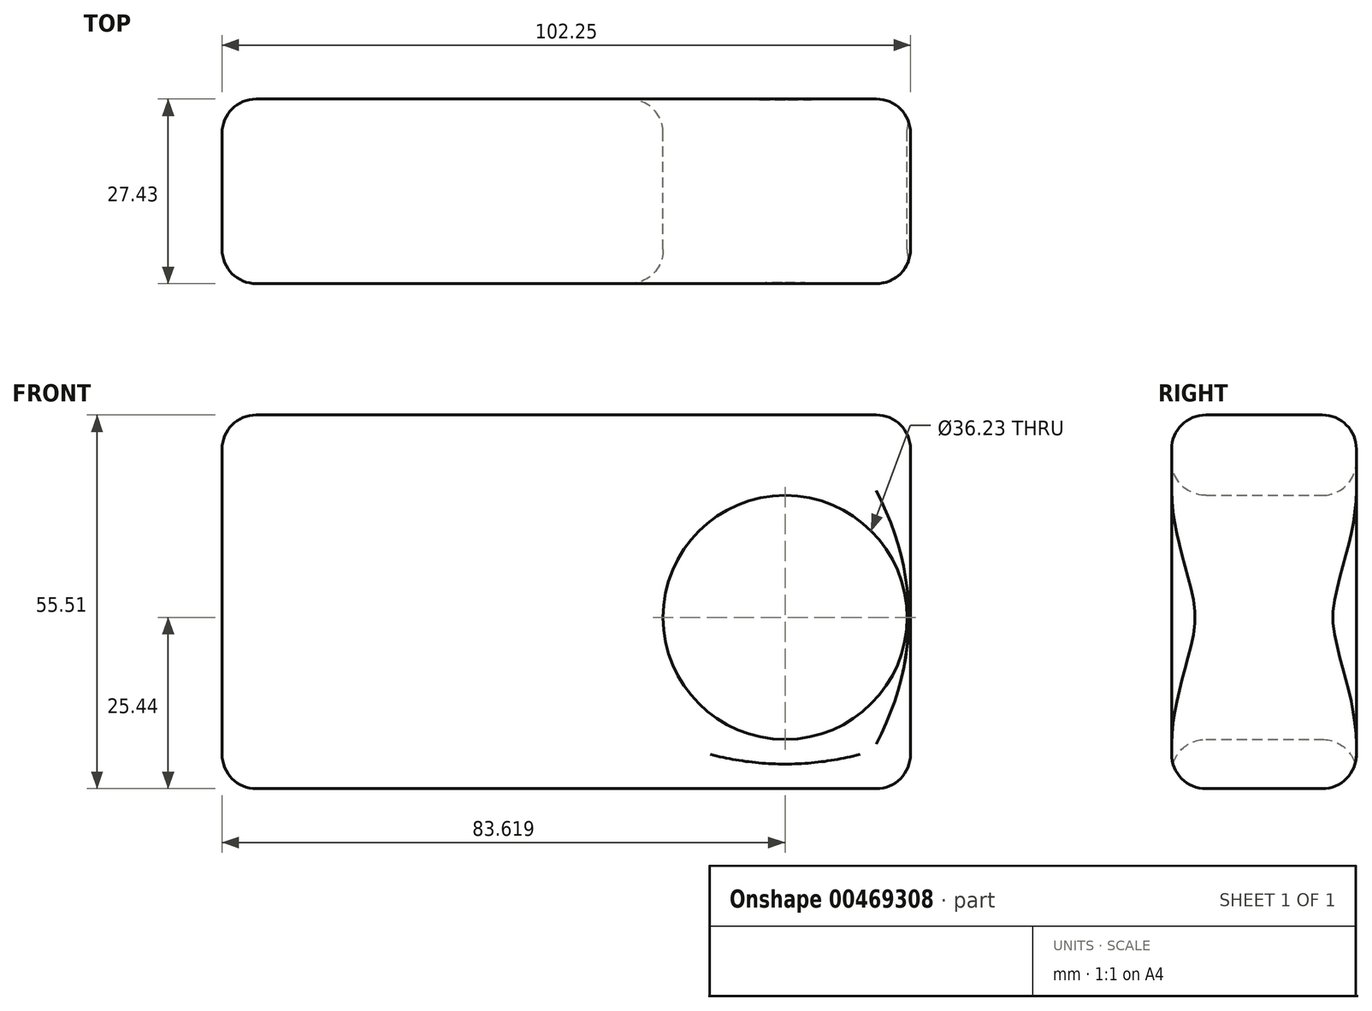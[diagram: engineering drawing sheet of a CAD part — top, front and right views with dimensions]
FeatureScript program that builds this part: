
annotation { "Feature Type Name" : "Feature", "Feature Type Description" : "" }
export const myFeature = defineFeature(function(context is Context, id is Id, definition is map)
    precondition{}
    {
        {
            var Q0;
            Q0=qCreatedBy(makeId("Front.planeOp"),FACE);
            var sketch = newSketch(context, id + "F0", { "sketchPlane" : qUnion([Q0])});
            skLineSegment(sketch, "E0.bottom", {"start": v(-64.67, 33.76) * mm, "end": v(37.58, 33.76) * mm});
            skLineSegment(sketch, "E0.top", {"start": v(-64.67, -21.75) * mm, "end": v(37.58, -21.75) * mm});
            skLineSegment(sketch, "E0.left", {"start": v(-64.67, 33.76) * mm, "end": v(-64.67, -21.75) * mm});
            skLineSegment(sketch, "E0.right", {"start": v(37.58, 33.76) * mm, "end": v(37.58, -21.75) * mm});
            skCircle(sketch, "E1", {"center": v(18.95, 3.7) * mm, "radius": 18.12 * mm});
            skSolve(sketch);
        }
        {
            var Q0;
            Q0 = qSketchRegion(id + "F0", true);
            extrude(context, id + "F1", {"entities" : qUnion([Q0]), "depth" : 27.43 * mm});
        }
        {
            var Q0;
            Q0=makeQuery(id+"F1.opExtrude","CAP_FACE",FACE,{"disambiguationData":[OSD([sQuery(id+"F0.wireOp",EDGE,"E0.bottom"),sQuery(id+"F0.wireOp",EDGE,"E0.top"),sQuery(id+"F0.wireOp",EDGE,"E0.left"),sQuery(id+"F0.wireOp",EDGE,"E0.right"),sQuery(id+"F0.wireOp",EDGE,"E1")])],"isStart":false});
            var Q1;
            Q1=makeQuery(id+"F1.opExtrude","SWEPT_FACE",FACE,{"disambiguationData":[OSD([sQuery(id+"F0.wireOp",EDGE,"E0.top")])]});
            var Q2;
            Q2=makeQuery(id+"F1.opExtrude","CAP_EDGE",EDGE,{"disambiguationData":[OSD([sQuery(id+"F0.wireOp",EDGE,"E0.bottom")])],"isStart":true});
            var Q3;
            Q3=makeQuery(id+"F1.opExtrude","CAP_EDGE",EDGE,{"disambiguationData":[OSD([sQuery(id+"F0.wireOp",EDGE,"E1")])],"isStart":false});
            var Q4;
            Q4=makeQuery(id+"F1.opExtrude","SWEPT_FACE",FACE,{"disambiguationData":[OSD([sQuery(id+"F0.wireOp",EDGE,"E0.left")])]});
            var Q5;
            Q5=makeQuery(id+"F1.opExtrude","SWEPT_EDGE",EDGE,{"disambiguationData":[OSD([sQuery(id+"F0.wireOp",EDGE,"E0.top"),sQuery(id+"F0.wireOp",EDGE,"E0.left")])]});
            var Q6;
            Q6=makeQuery(id+"F1.opExtrude","CAP_FACE",FACE,{"disambiguationData":[OSD([sQuery(id+"F0.wireOp",EDGE,"E0.bottom"),sQuery(id+"F0.wireOp",EDGE,"E0.top"),sQuery(id+"F0.wireOp",EDGE,"E0.left"),sQuery(id+"F0.wireOp",EDGE,"E0.right"),sQuery(id+"F0.wireOp",EDGE,"E1")])],"isStart":true});
            var Q7;
            Q7=makeQuery(id+"F1.opExtrude","SWEPT_EDGE",EDGE,{"disambiguationData":[OSD([sQuery(id+"F0.wireOp",EDGE,"E0.bottom"),sQuery(id+"F0.wireOp",EDGE,"E0.right")])]});
            var Q8;
            Q8=makeQuery(id+"F1.opExtrude","SWEPT_FACE",FACE,{"disambiguationData":[OSD([sQuery(id+"F0.wireOp",EDGE,"E0.right")])]});
            var Q9;
            Q9=makeQuery(id+"F1.opExtrude","SWEPT_FACE",FACE,{"disambiguationData":[OSD([sQuery(id+"F0.wireOp",EDGE,"E0.bottom")])]});
            var Q10;
            Q10=makeQuery(id+"F1.opExtrude","SWEPT_EDGE",EDGE,{"disambiguationData":[OSD([sQuery(id+"F0.wireOp",EDGE,"E0.bottom"),sQuery(id+"F0.wireOp",EDGE,"E0.left")])]});
            var Q11;
            Q11=makeQuery(id+"F1.opExtrude","SWEPT_FACE",FACE,{"disambiguationData":[OSD([sQuery(id+"F0.wireOp",EDGE,"E1")])]});
            var Q12;
            Q12=makeQuery(id+"F1.opExtrude","CAP_EDGE",EDGE,{"disambiguationData":[OSD([sQuery(id+"F0.wireOp",EDGE,"E0.left")])],"isStart":true});
            var Q13;
            Q13=makeQuery(id+"F1.opExtrude","CAP_EDGE",EDGE,{"disambiguationData":[OSD([sQuery(id+"F0.wireOp",EDGE,"E0.left")])],"isStart":false});
            var Q14;
            Q14=makeQuery(id+"F1.opExtrude","CAP_EDGE",EDGE,{"disambiguationData":[OSD([sQuery(id+"F0.wireOp",EDGE,"E1")])],"isStart":true});
            var Q15;
            Q15=makeQuery(id+"F1.opExtrude","SWEPT_EDGE",EDGE,{"disambiguationData":[OSD([sQuery(id+"F0.wireOp",EDGE,"E0.top"),sQuery(id+"F0.wireOp",EDGE,"E0.right")])]});
            var Q16;
            Q16=makeQuery(id+"F1.opExtrude","CAP_EDGE",EDGE,{"disambiguationData":[OSD([sQuery(id+"F0.wireOp",EDGE,"E0.bottom")])],"isStart":false});
            var Q17;
            Q17=makeQuery(id+"F1.opExtrude","CAP_EDGE",EDGE,{"disambiguationData":[OSD([sQuery(id+"F0.wireOp",EDGE,"E0.top")])],"isStart":true});
            var Q18;
            Q18=makeQuery(id+"F1.opExtrude","CAP_EDGE",EDGE,{"disambiguationData":[OSD([sQuery(id+"F0.wireOp",EDGE,"E0.top")])],"isStart":false});
            var Q19;
            Q19=makeQuery(id+"F1.opExtrude","CAP_EDGE",EDGE,{"disambiguationData":[OSD([sQuery(id+"F0.wireOp",EDGE,"E0.right")])],"isStart":true});
            var Q20;
            Q20=makeQuery(id+"F1.opExtrude","CAP_EDGE",EDGE,{"disambiguationData":[OSD([sQuery(id+"F0.wireOp",EDGE,"E0.right")])],"isStart":false});
            fillet(context, id + "F2", {"entities" : qUnion([Q0, Q1, Q2, Q3, Q4, Q5, Q6, Q7, Q8, Q9, Q10, Q11, Q12, Q13, Q14, Q15, Q16, Q17, Q18, Q19, Q20]), "radius" : 5.08 * mm, "tangentPropagation" : true, "allowEdgeOverflow" : false});
        }
    });
